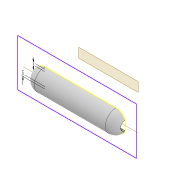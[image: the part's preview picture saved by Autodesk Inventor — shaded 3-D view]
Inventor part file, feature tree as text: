
AUTODESK INVENTOR PART (.ipt)
format: ipt  version: 2022 (Build 260153000, 153)  size: 361,472 bytes
history: native  units: mm
features: projected_geometry x10, extrude x9, sketch x9, fillet x3, plane x2, loft x1, other x1, revolve x1, chamfer x1
ambient origin geometry x8: Origin, YZ Plane, XZ Plane, XY Plane, X Axis, Y Axis, Z Axis, Center Point
bodies: Solid1 (feature_tree)
feature tree (37):
  extrude  "Extrusion1"  Depth=8.0mm
  extrude  "Extrusion2"  Depth=4.0mm
  plane  "Work Plane1"
  sketch  "Sketch3"  dims[d4=3.0mm d5=3.0mm d6=0.0mm d7=4.0mm]
  sketch  "Sketch5"  dims[d8=2.0mm d9=26.0mm]
  loft  "Loft2"
  fillet  "Fillet1"  [1 undecoded]
  fillet  "Fillet2"  Radius=4.0mm
  extrude  "Extrusion3"  Depth=26.0mm
  sketch  "Sketch7"  dims[d12=1.0mm d13=0.0mm]
  other  "Work Axis1"
  revolve  "Revolution1"  [1 undecoded]
  extrude  "Extrusion4"  TaperAngle=0.0deg  [1 undecoded]
  plane  "Work Plane3"
  extrude  "Extrusion5"  Depth=10.0mm
  fillet  "Fillet3"  Radius=5.0mm
  sketch  "Sketch10"  dims[d26=4.5mm d27=10.0mm d28=5.0mm d29=10.0mm d30=0.0mm d31=90.0deg d32=0.0mm d33=90.0deg d34=4.5mm d35=1.0mm d36=14.0mm d37=0.0mm d38=1.0mm d39=1.0mm d40=1.0mm d41=1.0mm d42=1.0mm d43=1.0mm d44=1.0mm d45=1.0mm d62=4.0mm d63=360.0deg d64=4.2mm d65=10.0mm d66=0.0mm d67=8.0mm d68=-16.5mm d69=4.0mm d70=4.0mm d71=4.0mm d72=4.0mm d73=4.0mm d74=0.5mm d75=0.0mm d76=4.0mm d77=1.0mm d78=1.0mm d79=17.5mm d80=0.0mm d81=1.4mm d82=0.0mm d85=0.0mm d86=0.0mm d87=1.2mm d88=0.0mm d89=0.4mm d90=2.0mm d91=45.0deg]
  extrude  "Unsuppress for Bottom Half (1/2)"  Depth=10.0mm
  extrude  "Unsuppress for Bottom Half (2/2)"  Depth=5.0mm
  extrude  "Unsuppress for Top Half (1/3)"  Depth=10.0mm
  extrude  "Unsuppress for Top Half (2/3)"  TaperAngle=0.0deg  [1 undecoded]
  chamfer  "Unsuppress for Top Half (3/3)"  Angle=90.0deg  [1 undecoded]
  sketch  "Sketch1"  dims[d0=4.0mm d1=8.0mm]
  sketch  "Sketch2"  dims[d2=4.0mm d3=4.0mm]
  projected_geometry  "Projected Loop1"
  sketch  "Sketch6"  dims[d10=26.0mm d11=5.0mm]
  projected_geometry  "Projected Loop4"
  projected_geometry  "Projected Loop5"
  projected_geometry  "Projected Loop6"
  projected_geometry  "Projected Loop7"
  sketch  "Sketch8"  dims[d14=22.0mm d15=0.0mm d16=10.0mm]
  sketch  "Sketch9"  dims[d17=14.0mm d18=28.0mm d19=0.0mm d20=0.0mm d21=5.0mm]
  projected_geometry  "Projected Loop8"
  projected_geometry  "Projected Loop9"
  projected_geometry  "Projected Loop10"
  projected_geometry  "Projected Loop11"
  projected_geometry  "Projected Loop12"
note: 5 required parameter values undecoded (feature->parameter linkage not recoverable at this tier; creation-order binding heuristic only, values carry confidence <= 0.55)